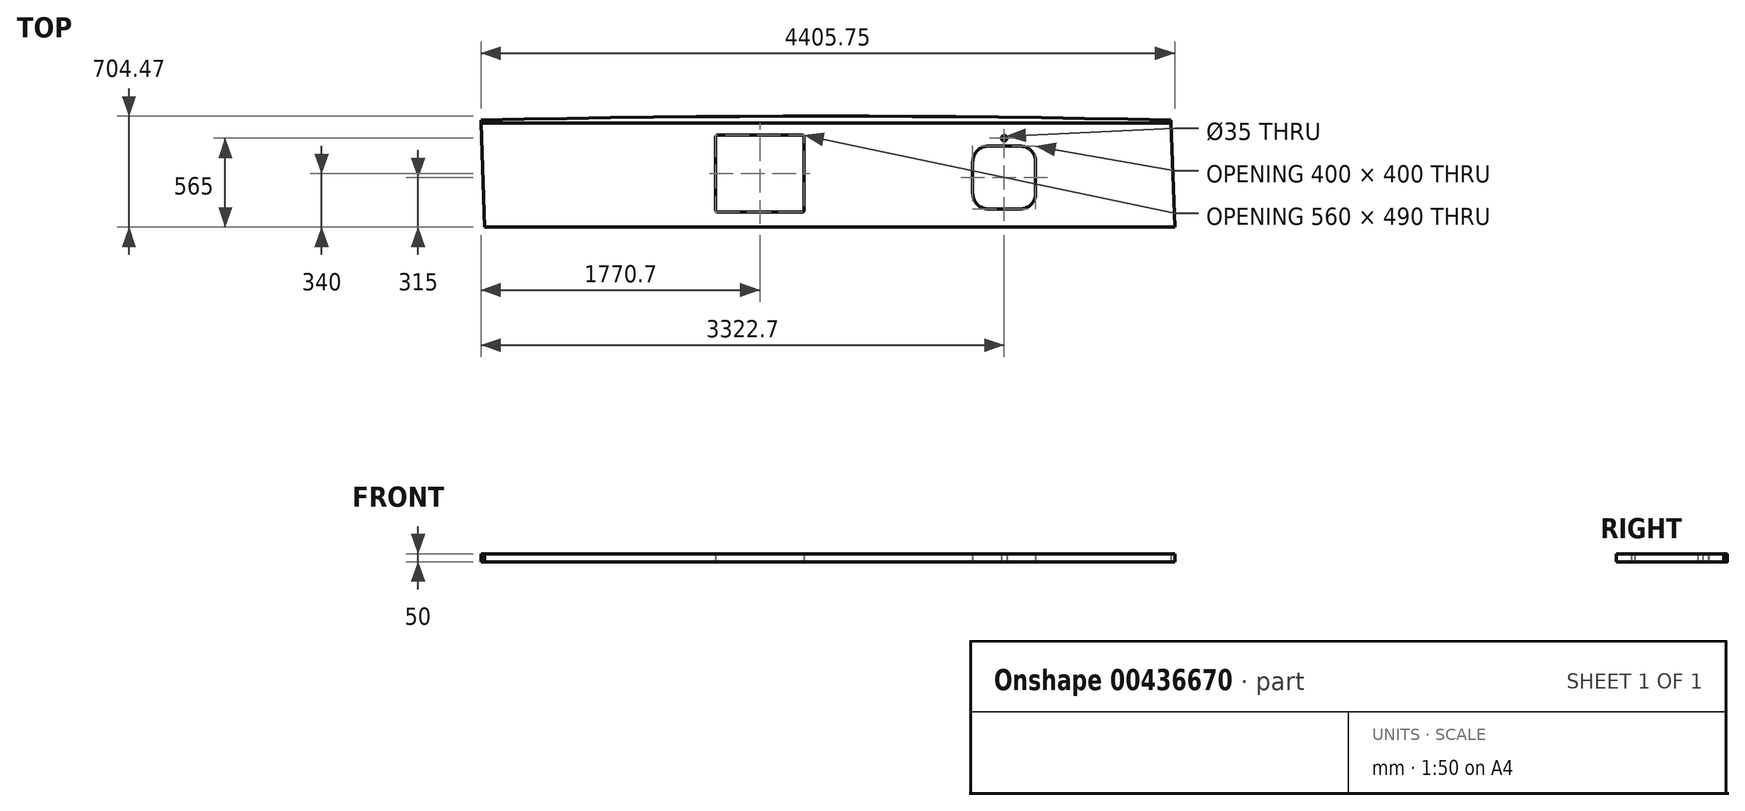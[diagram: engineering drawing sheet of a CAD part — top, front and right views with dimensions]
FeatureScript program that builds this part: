
annotation { "Feature Type Name" : "Feature", "Feature Type Description" : "" }
export const myFeature = defineFeature(function(context is Context, id is Id, definition is map)
    precondition{}
    {
        {
            var Q0;
            Q0=qCreatedBy(makeId("Top.planeOp"),FACE);
            var sketch = newSketch(context, id + "F0", { "sketchPlane" : qUnion([Q0])});
            skLineSegment(sketch, "E0.top", {"start": v(2185.5, 340) * mm, "end": v(-2196.5, 340) * mm});
            skPoint(sketch, "E0.middle", {"position": v(0, 0) * mm});
            skLineSegment(sketch, "E1.bottom", {"start": v(-696.5, 265) * mm, "end": v(-156.5, 265) * mm});
            skLineSegment(sketch, "E1.top", {"start": v(-696.5, -225) * mm, "end": v(-156.5, -225) * mm});
            skLineSegment(sketch, "E1.left", {"start": v(-706.5, 255) * mm, "end": v(-706.5, -215) * mm});
            skLineSegment(sketch, "E1.right", {"start": v(-146.5, 255) * mm, "end": v(-146.5, -215) * mm});
            skLineSegment(sketch, "E2.bottom", {"start": v(1025.5, 195) * mm, "end": v(1225.5, 195) * mm});
            skLineSegment(sketch, "E2.top", {"start": v(1025.5, -205) * mm, "end": v(1225.5, -205) * mm});
            skLineSegment(sketch, "E2.left", {"start": v(925.5, 95) * mm, "end": v(925.5, -105) * mm});
            skLineSegment(sketch, "E2.right", {"start": v(1325.5, 95) * mm, "end": v(1325.5, -105) * mm});
            skLineSegment(sketch, "E3", {"start": v(-426.5, 265) * mm, "end": v(-426.5, -225) * mm, "construction": true});
            skPoint(sketch, "E4.visualSharp", {"position": v(925.5, 195) * mm});
            skArc(sketch, "E4.filletArc", {"start": v(1025.5, 195) * mm, "mid": v(954.79, 165.71) * mm, "end": v(925.5, 95) * mm});
            skPoint(sketch, "E5.visualSharp", {"position": v(1325.5, 195) * mm});
            skArc(sketch, "E5.filletArc", {"start": v(1325.5, 95) * mm, "mid": v(1296.21, 165.71) * mm, "end": v(1225.5, 195) * mm});
            skPoint(sketch, "E6.visualSharp", {"position": v(1325.5, -205) * mm});
            skArc(sketch, "E6.filletArc", {"start": v(1225.5, -205) * mm, "mid": v(1296.21, -175.71) * mm, "end": v(1325.5, -105) * mm});
            skPoint(sketch, "E7.visualSharp", {"position": v(925.5, -205) * mm});
            skArc(sketch, "E7.filletArc", {"start": v(925.5, -105) * mm, "mid": v(954.79, -175.71) * mm, "end": v(1025.5, -205) * mm});
            skPoint(sketch, "E8.visualSharp", {"position": v(-706.5, 265) * mm});
            skArc(sketch, "E8.filletArc", {"start": v(-696.5, 265) * mm, "mid": v(-703.57, 262.07) * mm, "end": v(-706.5, 255) * mm});
            skPoint(sketch, "E9.visualSharp", {"position": v(-146.5, 265) * mm});
            skArc(sketch, "E9.filletArc", {"start": v(-146.5, 255) * mm, "mid": v(-149.43, 262.07) * mm, "end": v(-156.5, 265) * mm});
            skPoint(sketch, "E10.visualSharp", {"position": v(-706.5, -225) * mm});
            skArc(sketch, "E10.filletArc", {"start": v(-706.5, -215) * mm, "mid": v(-703.57, -222.07) * mm, "end": v(-696.5, -225) * mm});
            skPoint(sketch, "E11.visualSharp", {"position": v(-146.5, -225) * mm});
            skArc(sketch, "E11.filletArc", {"start": v(-156.5, -225) * mm, "mid": v(-149.43, -222.07) * mm, "end": v(-146.5, -215) * mm});
            skLineSegment(sketch, "E12", {"start": v(1125.5, 0) * mm, "end": v(1125.5, 325.05) * mm, "construction": true});
            skPoint(sketch, "E12.startSnap0", {"position": v(1125.5, -205) * mm});
            skCircle(sketch, "E13", {"center": v(1125.5, 245) * mm, "radius": 17.5 * mm});
            skLineSegment(sketch, "E14", {"start": v(-2197.2, 359.98) * mm, "end": v(-2173.45, -320) * mm});
            skLineSegment(sketch, "E15", {"start": v(2184.8, 360.02) * mm, "end": v(2208.55, -320) * mm});
            skLineSegment(sketch, "E16", {"start": v(-2173.45, -320) * mm, "end": v(2208.55, -320) * mm});
            skArc(sketch, "E17", {"start": v(2184.8, 360.02) * mm, "mid": v(-5.85, 384.47) * mm, "end": v(-2196.5, 360) * mm});
            skArc(sketch, "E18.extension", {"start": v(-2196.5, 360) * mm, "mid": v(-2196.85, 360) * mm, "end": v(-2197.2, 359.98) * mm});
            skSolve(sketch);
        }
        {
            var Q0;
            Q0 = qSketchRegion(id + "F0", true);
            extrude(context, id + "F1", {"entities" : qUnion([Q0]), "depth" : 50 * mm});
        }
        {
            var Q0;
            Q0=makeQuery(id+"F1.opExtrude","CAP_FACE",FACE,{"disambiguationData":[OSD([sQuery(id+"F0.wireOp",EDGE,"E1.bottom"),sQuery(id+"F0.wireOp",EDGE,"E1.top"),sQuery(id+"F0.wireOp",EDGE,"E1.left"),sQuery(id+"F0.wireOp",EDGE,"E1.right"),sQuery(id+"F0.wireOp",EDGE,"E2.bottom"),sQuery(id+"F0.wireOp",EDGE,"E2.top"),sQuery(id+"F0.wireOp",EDGE,"E2.left"),sQuery(id+"F0.wireOp",EDGE,"E2.right"),sQuery(id+"F0.wireOp",EDGE,"E4.filletArc"),sQuery(id+"F0.wireOp",EDGE,"E5.filletArc"),sQuery(id+"F0.wireOp",EDGE,"E6.filletArc"),sQuery(id+"F0.wireOp",EDGE,"E7.filletArc"),sQuery(id+"F0.wireOp",EDGE,"E8.filletArc"),sQuery(id+"F0.wireOp",EDGE,"E9.filletArc"),sQuery(id+"F0.wireOp",EDGE,"E10.filletArc"),sQuery(id+"F0.wireOp",EDGE,"E11.filletArc"),sQuery(id+"F0.wireOp",EDGE,"E13"),sQuery(id+"F0.wireOp",EDGE,"E14"),sQuery(id+"F0.wireOp",EDGE,"E15"),sQuery(id+"F0.wireOp",EDGE,"E16"),sQuery(id+"F0.wireOp",EDGE,"E17"),sQuery(id+"F0.wireOp",EDGE,"E18.extension")])],"isStart":false});
            var sketch = newSketch(context, id + "F2", { "sketchPlane" : qUnion([Q0])});
            skLineSegment(sketch, "E19", {"start": v(-2196.5, 340) * mm, "end": v(2184.8, 340) * mm});
            skLineSegment(sketch, "E20", {"start": v(-2196.5, 340) * mm, "end": v(-2304.12, 442.1) * mm});
            skLineSegment(sketch, "E21", {"start": v(-2304.12, 442.1) * mm, "end": v(2251.09, 442.1) * mm});
            skLineSegment(sketch, "E22", {"start": v(2251.09, 442.1) * mm, "end": v(2184.8, 340) * mm});
            skSolve(sketch);
        }
        {
            var Q0;
            Q0 = qSketchRegion(id + "F2", true);
            extrude(context, id + "F3", {"entities" : qUnion([Q0]), "operationType" : NewBodyOperationType.REMOVE, "oppositeDirection" : true, "depth" : 0.1 * mm});
        }
    });
